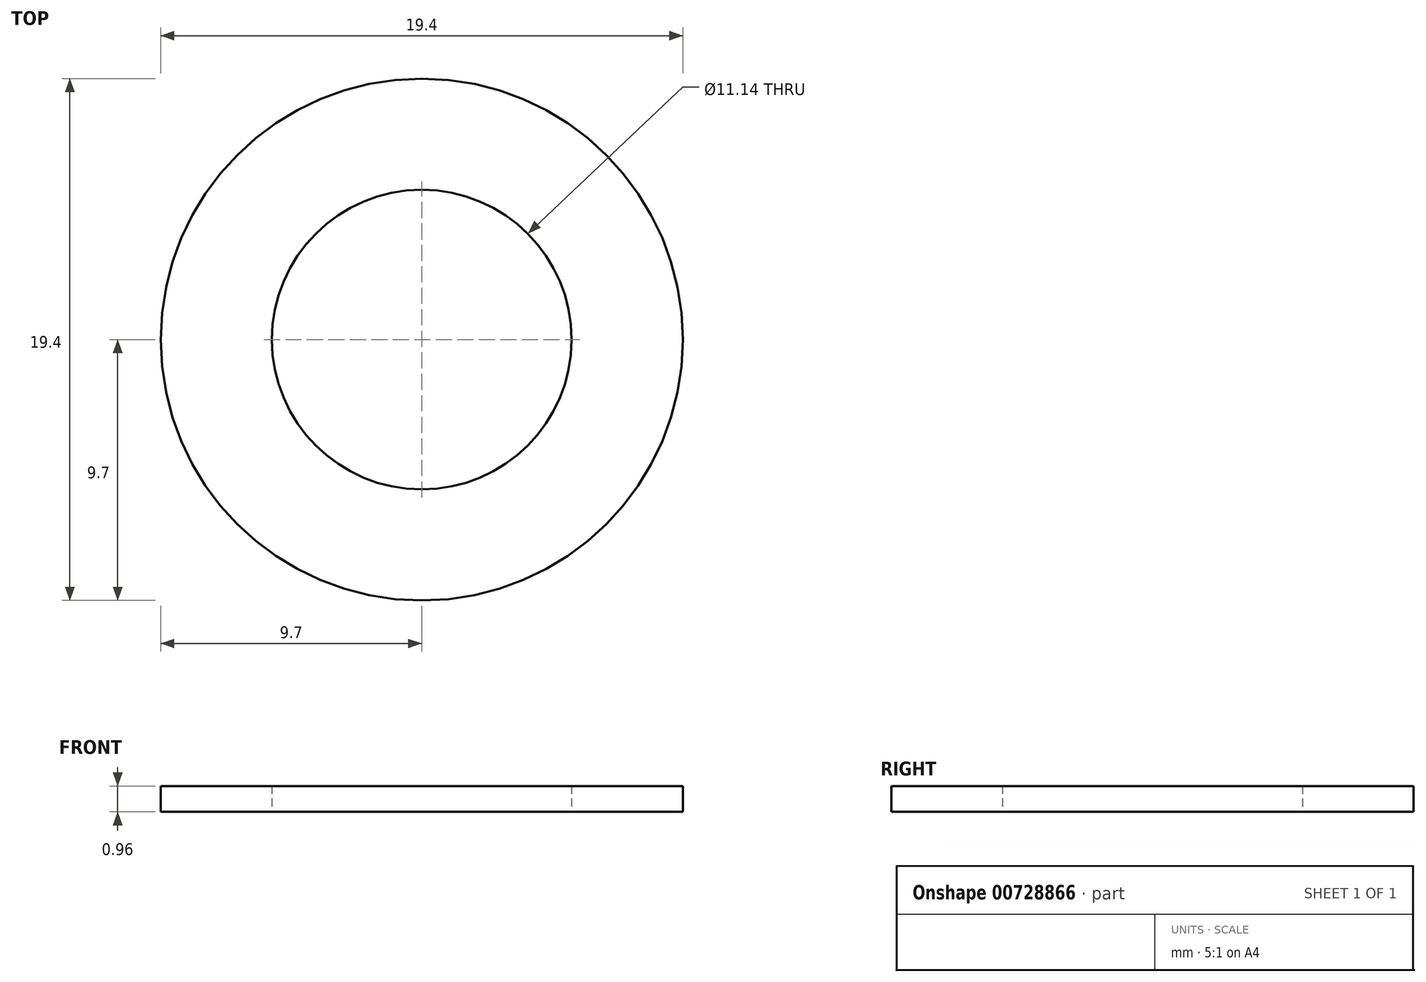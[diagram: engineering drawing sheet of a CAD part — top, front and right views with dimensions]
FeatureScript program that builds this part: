
annotation { "Feature Type Name" : "Feature", "Feature Type Description" : "" }
export const myFeature = defineFeature(function(context is Context, id is Id, definition is map)
    precondition{}
    {
        {
            var Q0;
            Q0=qCreatedBy(makeId("Top.planeOp"),FACE);
            var sketch = newSketch(context, id + "F0", { "sketchPlane" : qUnion([Q0])});
            skCircle(sketch, "E0", {"center": v(0, 0) * mm, "radius": 5.57 * mm});
            skCircle(sketch, "E1", {"center": v(0, 0) * mm, "radius": 9.7 * mm});
            skSolve(sketch);
        }
        {
            var Q0;
            Q0 = qSketchRegion(id + "F0", true);
            extrude(context, id + "F1", {"entities" : qUnion([Q0]), "depth" : .96 * mm, "offsetDistance" : 25.4 * mm});
        }
    });
